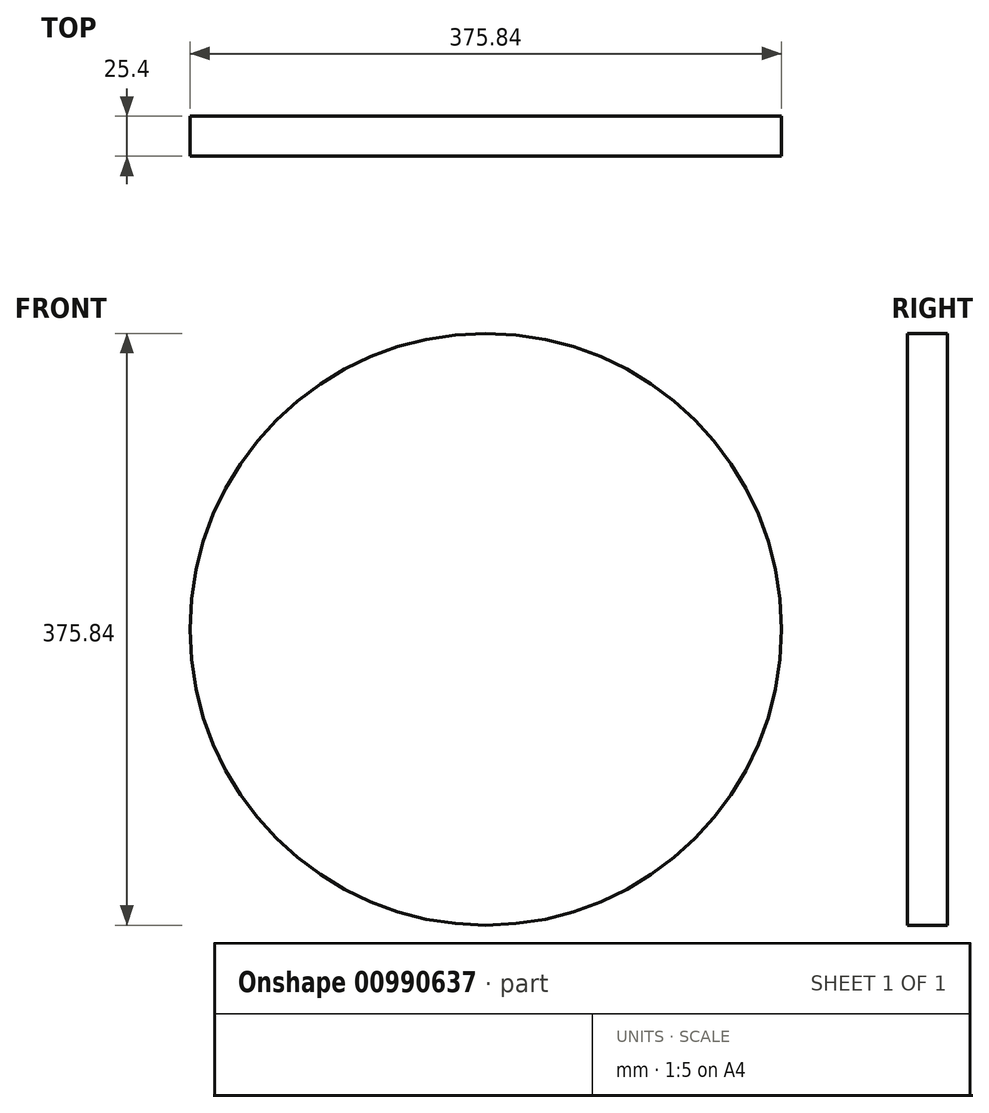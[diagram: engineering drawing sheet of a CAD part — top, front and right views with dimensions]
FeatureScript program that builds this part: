
annotation { "Feature Type Name" : "Feature", "Feature Type Description" : "" }
export const myFeature = defineFeature(function(context is Context, id is Id, definition is map)
    precondition{}
    {
        {
            var Q0;
            Q0=qCreatedBy(makeId("Front.planeOp"),FACE);
            var sketch = newSketch(context, id + "F0", { "sketchPlane" : qUnion([Q0])});
            skCircle(sketch, "E0", {"center": v(-54.1, -222.54) * mm, "radius": 187.92 * mm});
            skSolve(sketch);
        }
        {
            var Q0;
            Q0=makeQuery(id+"F0.imprint","IMPRINT",FACE,{"disambiguationData":[TD([[makeQuery(id+"F0.imprint","IMPRINT",EDGE,{"derivedFrom":sQuery(id+"F0.wireOp",EDGE,"E0")}),1.0]])]});
            extrude(context, id + "F1", {"entities" : qUnion([Q0]), "depth" : 25.4 * mm, "offsetDistance" : 25.4 * mm});
        }
    });
